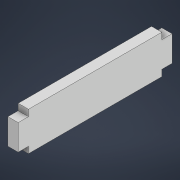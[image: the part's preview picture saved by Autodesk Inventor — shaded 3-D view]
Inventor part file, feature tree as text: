
AUTODESK INVENTOR PART (.ipt)
format: ipt  version: 2022 (Build 260153000, 153)  size: 100,352 bytes
history: native  units: mm
features: other x1, extrude x1, sketch x1
ambient origin geometry x8: Origin, YZ Plane, XZ Plane, XY Plane, X Axis, Y Axis, Z Axis, Center Point
bodies: Body1 (feature_tree)
feature tree (3):
  other  "Твердое тело1"
  extrude  "Выдавливание1"  Depth=15.0mm
  sketch  "Эскиз1"
